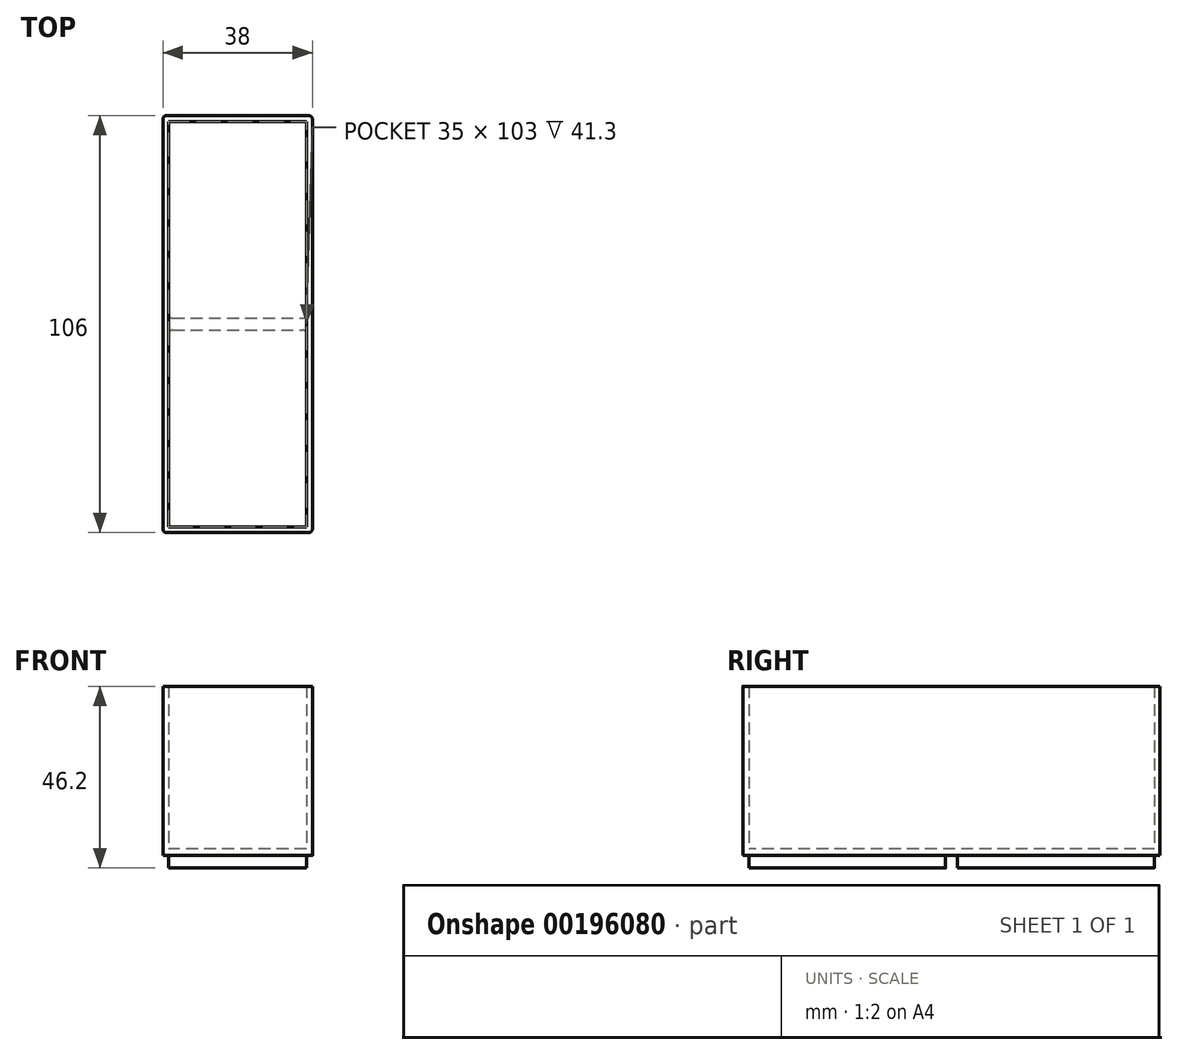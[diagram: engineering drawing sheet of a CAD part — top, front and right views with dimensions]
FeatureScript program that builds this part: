
annotation { "Feature Type Name" : "Feature", "Feature Type Description" : "" }
export const myFeature = defineFeature(function(context is Context, id is Id, definition is map)
    precondition{}
    {
        {
            var Q0;
            Q0=qCreatedBy(makeId("Top.planeOp"),FACE);
            var sketch = newSketch(context, id + "F0", { "sketchPlane" : qUnion([Q0])});
            skLineSegment(sketch, "E0.bottom", {"start": v(0, 0) * mm, "end": v(38, 0) * mm});
            skLineSegment(sketch, "E0.top", {"start": v(0, 53) * mm, "end": v(38, 53) * mm});
            skLineSegment(sketch, "E0.left", {"start": v(0, 0) * mm, "end": v(0, 53) * mm});
            skLineSegment(sketch, "E0.right", {"start": v(38, 0) * mm, "end": v(38, 53) * mm});
            skLineSegment(sketch, "E1.bottom", {"start": v(1.5, 1.5) * mm, "end": v(36.5, 1.5) * mm});
            skLineSegment(sketch, "E1.top", {"start": v(1.5, 51.5) * mm, "end": v(36.5, 51.5) * mm});
            skLineSegment(sketch, "E1.left", {"start": v(1.5, 1.5) * mm, "end": v(1.5, 51.5) * mm});
            skLineSegment(sketch, "E1.right", {"start": v(36.5, 1.5) * mm, "end": v(36.5, 51.5) * mm});
            skLineSegment(sketch, "E2.top", {"start": v(0, 106) * mm, "end": v(38, 106) * mm});
            skLineSegment(sketch, "E2.left", {"start": v(0, 53) * mm, "end": v(0, 106) * mm});
            skLineSegment(sketch, "E2.right", {"start": v(38, 53) * mm, "end": v(38, 106) * mm});
            skLineSegment(sketch, "E3.bottom", {"start": v(1.5, 54.5) * mm, "end": v(36.5, 54.5) * mm});
            skLineSegment(sketch, "E3.top", {"start": v(1.5, 104.5) * mm, "end": v(36.5, 104.5) * mm});
            skLineSegment(sketch, "E3.left", {"start": v(1.5, 54.5) * mm, "end": v(1.5, 104.5) * mm});
            skLineSegment(sketch, "E3.right", {"start": v(36.5, 54.5) * mm, "end": v(36.5, 104.5) * mm});
            skLineSegment(sketch, "E4", {"start": v(36.5, 51.5) * mm, "end": v(36.5, 54.5) * mm});
            skLineSegment(sketch, "E5", {"start": v(1.5, 51.5) * mm, "end": v(1.5, 54.5) * mm});
            skSolve(sketch);
        }
        {
            var Q0;
            Q0=makeQuery(id+"F0.imprint","IMPRINT",FACE,{"disambiguationData":[TD([[makeQuery(id+"F0.imprint","IMPRINT",EDGE,{"derivedFrom":sQuery(id+"F0.wireOp",EDGE,"E3.bottom")}),1.0]])]});
            var Q1;
            Q1=makeQuery(id+"F0.imprint","IMPRINT",FACE,{"disambiguationData":[TD([[makeQuery(id+"F0.imprint","IMPRINT",EDGE,{"derivedFrom":sQuery(id+"F0.wireOp",EDGE,"E1.bottom")}),1.0]])]});
            extrude(context, id + "F1", {"entities" : qUnion([Q0, Q1]), "oppositeDirection" : true, "depth" : 3.2 * mm, "offsetDistance" : 25 * mm});
        }
        {
            var Q0;
            Q0=makeQuery(id+"F0.imprint","IMPRINT",FACE,{"disambiguationData":[TD([[makeQuery(id+"F0.imprint","IMPRINT",EDGE,{"derivedFrom":sQuery(id+"F0.wireOp",EDGE,"E0.top")}),1.0]])]});
            var Q1;
            Q1=makeQuery(id+"F0.imprint","IMPRINT",FACE,{"disambiguationData":[TD([[makeQuery(id+"F0.imprint","IMPRINT",EDGE,{"derivedFrom":sQuery(id+"F0.wireOp",EDGE,"E0.bottom")}),1.0]])]});
            var Q2;
            Q2=makeQuery(id+"F0.imprint","IMPRINT",FACE,{"disambiguationData":[TD([[makeQuery(id+"F0.imprint","IMPRINT",EDGE,{"derivedFrom":sQuery(id+"F0.wireOp",EDGE,"E1.bottom")}),1.0]])]});
            var Q3;
            Q3=makeQuery(id+"F0.imprint","IMPRINT",FACE,{"disambiguationData":[TD([[makeQuery(id+"F0.imprint","IMPRINT",EDGE,{"derivedFrom":sQuery(id+"F0.wireOp",EDGE,"E3.bottom")}),1.0]])]});
            var Q4;
            {var subQ5=sQuery(id+"F0.wireOp",EDGE,"E3.bottom");Q4=makeQuery(id+"F0.imprint","IMPRINT",FACE,{"disambiguationData":[TD([[makeQuery(id+"F0.imprint","IMPRINT",EDGE,{"derivedFrom":subQ5}),-1.0]])]});}
            var Q5;
            {var subQ0=sQuery(id+"F0.wireOp",EDGE,"E1.top");Q5=makeQuery(id+"F0.imprint","IMPRINT",FACE,{"disambiguationData":[TD([[makeQuery(id+"F0.imprint","IMPRINT",EDGE,{"derivedFrom":subQ0}),1.0]])]});}
            extrude(context, id + "F2", {"entities" : qUnion([Q0, Q1, Q2, Q3, Q4, Q5]), "operationType" : NewBodyOperationType.ADD, "depth" : 1.7 * mm, "offsetDistance" : 25 * mm});
        }
        {
            var Q0;
            Q0=makeQuery(id+"F0.imprint","IMPRINT",FACE,{"disambiguationData":[TD([[makeQuery(id+"F0.imprint","IMPRINT",EDGE,{"derivedFrom":sQuery(id+"F0.wireOp",EDGE,"E2.top")}),-1.0]])]});
            var Q1;
            Q1=makeQuery(id+"F0.imprint","IMPRINT",FACE,{"disambiguationData":[TD([[makeQuery(id+"F0.imprint","IMPRINT",EDGE,{"derivedFrom":sQuery(id+"F0.wireOp",EDGE,"E0.bottom")}),1.0]])]});
            extrude(context, id + "F3", {"entities" : qUnion([Q0, Q1]), "operationType" : NewBodyOperationType.ADD, "depth" : 43 * mm, "offsetDistance" : 25 * mm});
        }
        {
            var Q0;
            {var subQ0=sQuery(id+"F0.wireOp",EDGE,"E0.left");var subQ1=sQuery(id+"F0.wireOp",EDGE,"E0.bottom");Q0=makeQuery(id+"F3.boolean.opBoolean","MERGE",EDGE,{"derivedFrom":[makeQuery(id+"F2.opExtrude","SWEPT_EDGE",EDGE,{"disambiguationData":[OSD([subQ1,subQ0])]}),makeQuery(id+"F3.opExtrude","SWEPT_EDGE",EDGE,{"disambiguationData":[OSD([subQ1,subQ0])]})]});}
            var Q1;
            {var subQ0=sQuery(id+"F0.wireOp",EDGE,"E0.right");var subQ1=sQuery(id+"F0.wireOp",EDGE,"E0.bottom");Q1=makeQuery(id+"F3.boolean.opBoolean","MERGE",EDGE,{"derivedFrom":[makeQuery(id+"F2.opExtrude","SWEPT_EDGE",EDGE,{"disambiguationData":[OSD([subQ1,subQ0])]}),makeQuery(id+"F3.opExtrude","SWEPT_EDGE",EDGE,{"disambiguationData":[OSD([subQ1,subQ0])]})]});}
            var Q2;
            {var subQ0=sQuery(id+"F0.wireOp",EDGE,"E2.right");var subQ1=sQuery(id+"F0.wireOp",EDGE,"E2.top");Q2=makeQuery(id+"F3.boolean.opBoolean","MERGE",EDGE,{"derivedFrom":[makeQuery(id+"F2.opExtrude","SWEPT_EDGE",EDGE,{"disambiguationData":[OSD([subQ1,subQ0])]}),makeQuery(id+"F3.opExtrude","SWEPT_EDGE",EDGE,{"disambiguationData":[OSD([subQ1,subQ0])]})]});}
            var Q3;
            {var subQ0=sQuery(id+"F0.wireOp",EDGE,"E2.left");var subQ1=sQuery(id+"F0.wireOp",EDGE,"E2.top");Q3=makeQuery(id+"F3.boolean.opBoolean","MERGE",EDGE,{"derivedFrom":[makeQuery(id+"F2.opExtrude","SWEPT_EDGE",EDGE,{"disambiguationData":[OSD([subQ1,subQ0])]}),makeQuery(id+"F3.opExtrude","SWEPT_EDGE",EDGE,{"disambiguationData":[OSD([subQ1,subQ0])]})]});}
            var Q4;
            Q4=makeQuery(id+"F1.opExtrude","SWEPT_EDGE",EDGE,{"disambiguationData":[OSD([sQuery(id+"F0.wireOp",EDGE,"E3.top"),sQuery(id+"F0.wireOp",EDGE,"E3.left")])]});
            var Q5;
            Q5=makeQuery(id+"F1.opExtrude","SWEPT_EDGE",EDGE,{"disambiguationData":[OSD([sQuery(id+"F0.wireOp",EDGE,"E3.top"),sQuery(id+"F0.wireOp",EDGE,"E3.right")])]});
            var Q6;
            Q6=makeQuery(id+"F1.opExtrude","SWEPT_EDGE",EDGE,{"disambiguationData":[OSD([sQuery(id+"F0.wireOp",EDGE,"E3.bottom"),sQuery(id+"F0.wireOp",EDGE,"E3.right"),sQuery(id+"F0.wireOp",EDGE,"E4")])]});
            var Q7;
            Q7=makeQuery(id+"F1.opExtrude","SWEPT_EDGE",EDGE,{"disambiguationData":[OSD([sQuery(id+"F0.wireOp",EDGE,"E3.bottom"),sQuery(id+"F0.wireOp",EDGE,"E3.left"),sQuery(id+"F0.wireOp",EDGE,"E5")])]});
            var Q8;
            Q8=makeQuery(id+"F1.opExtrude","SWEPT_EDGE",EDGE,{"disambiguationData":[OSD([sQuery(id+"F0.wireOp",EDGE,"E1.top"),sQuery(id+"F0.wireOp",EDGE,"E1.left"),sQuery(id+"F0.wireOp",EDGE,"E5")])]});
            var Q9;
            Q9=makeQuery(id+"F1.opExtrude","SWEPT_EDGE",EDGE,{"disambiguationData":[OSD([sQuery(id+"F0.wireOp",EDGE,"E1.top"),sQuery(id+"F0.wireOp",EDGE,"E1.right"),sQuery(id+"F0.wireOp",EDGE,"E4")])]});
            var Q10;
            Q10=makeQuery(id+"F1.opExtrude","SWEPT_EDGE",EDGE,{"disambiguationData":[OSD([sQuery(id+"F0.wireOp",EDGE,"E1.bottom"),sQuery(id+"F0.wireOp",EDGE,"E1.right")])]});
            var Q11;
            Q11=makeQuery(id+"F1.opExtrude","SWEPT_EDGE",EDGE,{"disambiguationData":[OSD([sQuery(id+"F0.wireOp",EDGE,"E1.bottom"),sQuery(id+"F0.wireOp",EDGE,"E1.left")])]});
            fillet(context, id + "F4", {"entities" : qUnion([Q0, Q1, Q2, Q3, Q4, Q5, Q6, Q7, Q8, Q9, Q10, Q11]), "radius" : 1 * mm, "tangentPropagation" : true, "allowEdgeOverflow" : false});
        }
    });
